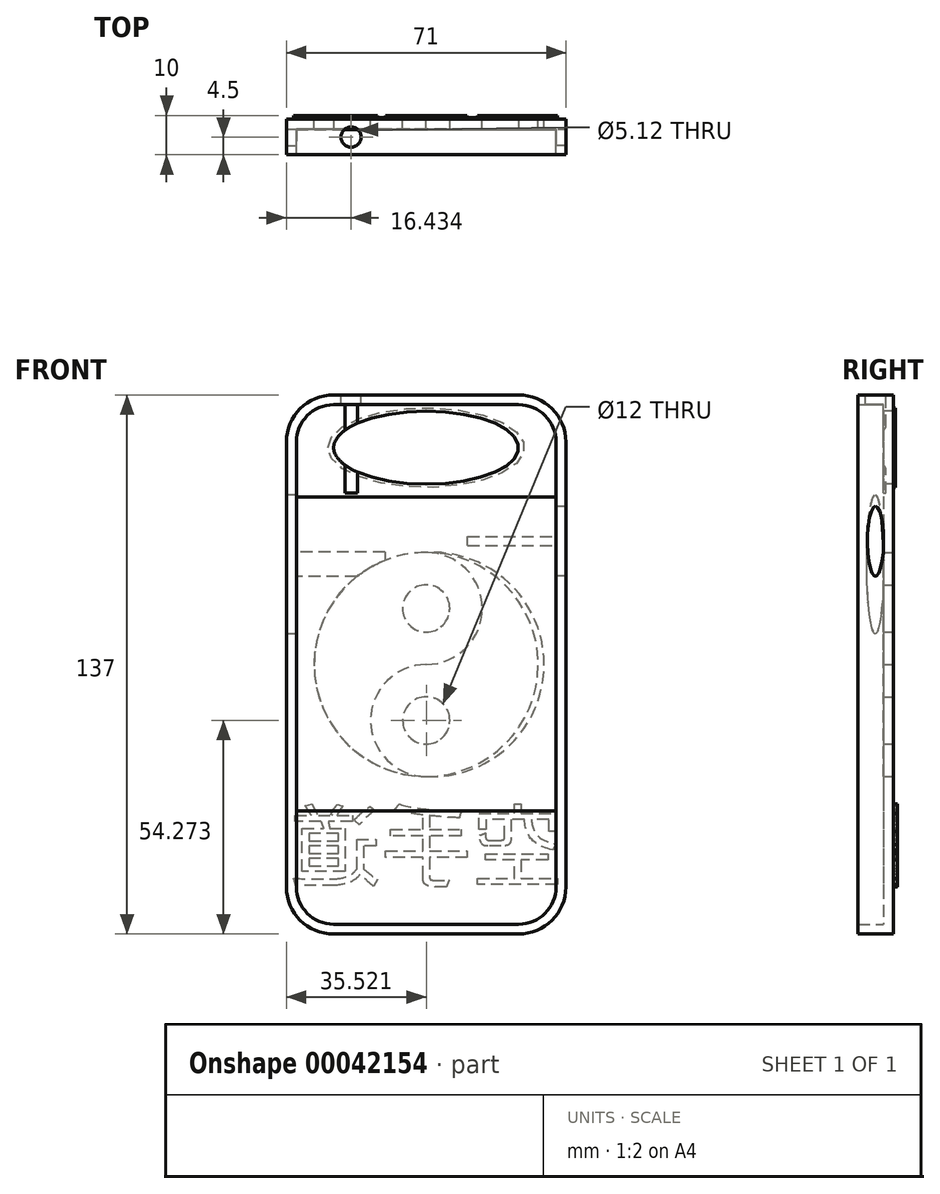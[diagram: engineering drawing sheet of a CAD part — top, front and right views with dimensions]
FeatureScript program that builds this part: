
annotation { "Feature Type Name" : "Feature", "Feature Type Description" : "" }
export const myFeature = defineFeature(function(context is Context, id is Id, definition is map)
    precondition{}
    {
        {
            var Q0;
            Q0=qCreatedBy(makeId("Front.planeOp"),FACE);
            var sketch = newSketch(context, id + "F0", { "sketchPlane" : qUnion([Q0])});
            skLineSegment(sketch, "E0.rect.bottom", {"start": v(35.5, 68.5) * mm, "end": v(-35.5, 68.5) * mm});
            skLineSegment(sketch, "E0.rect.top", {"start": v(35.5, -68.5) * mm, "end": v(-35.5, -68.5) * mm});
            skLineSegment(sketch, "E0.rect.left", {"start": v(35.5, 68.5) * mm, "end": v(35.5, -68.5) * mm});
            skLineSegment(sketch, "E0.rect.right", {"start": v(-35.5, 68.5) * mm, "end": v(-35.5, -68.5) * mm});
            skPoint(sketch, "E0.rect.middle", {"position": v(0, 0) * mm});
            skSolve(sketch);
        }
        {
            var Q0;
            Q0=makeQuery(id+"F0.imprint","IMPRINT",FACE,{"disambiguationData":[TD([[makeQuery(id+"F0.imprint","IMPRINT",EDGE,{"derivedFrom":sQuery(id+"F0.wireOp",EDGE,"E0.rect.bottom")}),1.0]])]});
            extrude(context, id + "F1", {"entities" : qUnion([Q0]), "depth" : 9 * mm});
        }
        {
            var Q0;
            Q0=makeQuery(id+"F1.opExtrude","SWEPT_EDGE",EDGE,{"disambiguationData":[OSD([sQuery(id+"F0.wireOp",EDGE,"E0.rect.bottom"),sQuery(id+"F0.wireOp",EDGE,"E0.rect.left")])]});
            var Q1;
            Q1=makeQuery(id+"F1.opExtrude","SWEPT_EDGE",EDGE,{"disambiguationData":[OSD([sQuery(id+"F0.wireOp",EDGE,"E0.rect.bottom"),sQuery(id+"F0.wireOp",EDGE,"E0.rect.right")])]});
            var Q2;
            Q2=makeQuery(id+"F1.opExtrude","SWEPT_EDGE",EDGE,{"disambiguationData":[OSD([sQuery(id+"F0.wireOp",EDGE,"E0.rect.top"),sQuery(id+"F0.wireOp",EDGE,"E0.rect.left")])]});
            var Q3;
            Q3=makeQuery(id+"F1.opExtrude","SWEPT_EDGE",EDGE,{"disambiguationData":[OSD([sQuery(id+"F0.wireOp",EDGE,"E0.rect.top"),sQuery(id+"F0.wireOp",EDGE,"E0.rect.right")])]});
            fillet(context, id + "F2", {"entities" : qUnion([Q0, Q1, Q2, Q3]), "radius" : 12 * mm, "tangentPropagation" : true, "allowEdgeOverflow" : false});
        }
        {
            var Q0;
            Q0=makeQuery(id+"F1.opExtrude","CAP_FACE",FACE,{"disambiguationData":[OSD([sQuery(id+"F0.wireOp",EDGE,"E0.rect.bottom"),sQuery(id+"F0.wireOp",EDGE,"E0.rect.top"),sQuery(id+"F0.wireOp",EDGE,"E0.rect.left"),sQuery(id+"F0.wireOp",EDGE,"E0.rect.right")])],"isStart":false});
            shell(context, id + "F3", {"entities" : qUnion([Q0]), "thickness" : 2.5 * mm});
        }
        {
            var Q0;
            Q0=makeQuery(id+"F1.opExtrude","SWEPT_FACE",FACE,{"disambiguationData":[OSD([sQuery(id+"F0.wireOp",EDGE,"E0.rect.bottom")])]});
            var sketch = newSketch(context, id + "F4", { "sketchPlane" : qUnion([Q0])});
            skLineSegment(sketch, "E1", {"start": v(0, 0) * mm, "end": v(0, -9) * mm});
            skLineSegment(sketch, "E2", {"start": v(-35.72, -4.5) * mm, "end": v(0, -4.5) * mm});
            skPoint(sketch, "E2.startSnap0", {"position": v(-23.5, -4.5) * mm});
            skPoint(sketch, "E3", {"position": v(-19.07, -4.5) * mm});
            skCircle(sketch, "E4", {"center": v(-19.07, -4.5) * mm, "radius": 2.56 * mm});
            skSolve(sketch);
        }
        {
            var Q0;
            Q0 = qSketchRegion(id + "F4", true);
            extrude(context, id + "F5", {"entities" : qUnion([Q0]), "operationType" : NewBodyOperationType.REMOVE, "oppositeDirection" : true, "depth" : 25 * mm});
        }
        {
            var Q0;
            Q0=makeQuery(id+"F1.opExtrude","SWEPT_FACE",FACE,{"disambiguationData":[OSD([sQuery(id+"F0.wireOp",EDGE,"E0.rect.right")])]});
            var sketch = newSketch(context, id + "F6", { "sketchPlane" : qUnion([Q0])});
            skEllipse(sketch, "E5", {"center": v(4.62, 25.44) * mm, "majorRadius": 17.66 * mm, "minorRadius": 2.16 * mm, "majorAxis": v(0, 1)});
            skSolve(sketch);
        }
        {
            var Q0;
            Q0 = qSketchRegion(id + "F6", true);
            extrude(context, id + "F7", {"entities" : qUnion([Q0]), "operationType" : NewBodyOperationType.REMOVE, "oppositeDirection" : true, "depth" : 25 * mm});
        }
        {
            var Q0;
            Q0=makeQuery(id+"F1.opExtrude","CAP_FACE",FACE,{"disambiguationData":[OSD([sQuery(id+"F0.wireOp",EDGE,"E0.rect.bottom"),sQuery(id+"F0.wireOp",EDGE,"E0.rect.top"),sQuery(id+"F0.wireOp",EDGE,"E0.rect.left"),sQuery(id+"F0.wireOp",EDGE,"E0.rect.right")])],"isStart":true});
            var sketch = newSketch(context, id + "F8", { "sketchPlane" : qUnion([Q0])});
            skEllipse(sketch, "E6", {"center": v(0, 55.09) * mm, "majorRadius": 23.5 * mm, "minorRadius": 9.28 * mm, "majorAxis": v(1, 0)});
            skEllipse(sketch, "E7", {"center": v(0, 55.09) * mm, "majorRadius": 24.96 * mm, "minorRadius": 10.1 * mm, "majorAxis": v(1, 0)});
            skSolve(sketch);
        }
        {
            var Q0;
            Q0=makeQuery(id+"F8.imprint","IMPRINT",FACE,{"disambiguationData":[TD([[makeQuery(id+"F8.imprint","IMPRINT",EDGE,{"derivedFrom":sQuery(id+"F8.wireOp",EDGE,"E6")}),-1.0]])]});
            extrude(context, id + "F9", {"entities" : qUnion([Q0]), "operationType" : NewBodyOperationType.ADD, "depth" : 0.5 * mm});
        }
        {
            var Q0;
            Q0=makeQuery(id+"F9.boolean.opBoolean","SPLIT",FACE,{"disambiguationData":[TD([makeQuery(id+"F9.opExtrude","SWEPT_FACE",FACE,{"disambiguationData":[OSD([sQuery(id+"F8.wireOp",EDGE,"E6")])]})])],"derivedFrom":makeQuery(id+"F1.opExtrude","CAP_FACE",FACE,{"disambiguationData":[OSD([sQuery(id+"F0.wireOp",EDGE,"E0.rect.bottom"),sQuery(id+"F0.wireOp",EDGE,"E0.rect.top"),sQuery(id+"F0.wireOp",EDGE,"E0.rect.left"),sQuery(id+"F0.wireOp",EDGE,"E0.rect.right")])],"isStart":true})});
            extrude(context, id + "F10", {"entities" : qUnion([Q0]), "operationType" : NewBodyOperationType.REMOVE, "oppositeDirection" : true, "depth" : 25 * mm});
        }
        {
            var Q0;
            Q0=makeQuery(id+"F1.opExtrude","SWEPT_FACE",FACE,{"disambiguationData":[OSD([sQuery(id+"F0.wireOp",EDGE,"E0.rect.left")])]});
            var sketch = newSketch(context, id + "F11", { "sketchPlane" : qUnion([Q0])});
            skEllipse(sketch, "E8", {"center": v(-4.56, 31.33) * mm, "majorRadius": 8.87 * mm, "minorRadius": 2.08 * mm, "majorAxis": v(0, 1)});
            skSolve(sketch);
        }
        {
            var Q0;
            Q0 = qSketchRegion(id + "F11", true);
            extrude(context, id + "F12", {"entities" : qUnion([Q0]), "operationType" : NewBodyOperationType.REMOVE, "oppositeDirection" : true, "depth" : 25 * mm});
        }
        {
            var Q0;
            {var subQ0=sQuery(id+"F0.wireOp",EDGE,"E0.rect.bottom");var subQ1=sQuery(id+"F0.wireOp",EDGE,"E0.rect.top");var subQ2=sQuery(id+"F0.wireOp",EDGE,"E0.rect.left");var subQ3=sQuery(id+"F0.wireOp",EDGE,"E0.rect.right");Q0=makeQuery(id+"F9.boolean.opBoolean","SPLIT",FACE,{"disambiguationData":[TD([makeQuery(id+"F1.opExtrude","SWEPT_FACE",FACE,{"disambiguationData":[OSD([subQ0])]})])],"derivedFrom":makeQuery(id+"F1.opExtrude","CAP_FACE",FACE,{"disambiguationData":[OSD([subQ0,subQ1,subQ2,subQ3])],"isStart":true})});}
            var sketch = newSketch(context, id + "F13", { "sketchPlane" : qUnion([Q0])});
            skArc(sketch, "E9", {"start": v(0, 28.45) * mm, "mid": v(-28.45, 0) * mm, "end": v(0, -28.45) * mm});
            skLineSegment(sketch, "E10", {"start": v(0, 28.45) * mm, "end": v(0, -28.45) * mm, "construction": true});
            skArc(sketch, "E11", {"start": v(0, 0) * mm, "mid": v(14.23, 14.23) * mm, "end": v(0, 28.45) * mm, "construction": true});
            skArc(sketch, "E12", {"start": v(0, 0) * mm, "mid": v(-14.25, -14.23) * mm, "end": v(0, -28.45) * mm, "construction": true});
            skArc(sketch, "E13", {"start": v(0, 28.45) * mm, "mid": v(-14.23, 14.23) * mm, "end": v(0, 0) * mm});
            skArc(sketch, "E14", {"start": v(0, -28.45) * mm, "mid": v(14.12, -14.23) * mm, "end": v(0, 0) * mm});
            skCircle(sketch, "E15", {"center": v(0, 14.23) * mm, "radius": 6 * mm});
            skCircle(sketch, "E16", {"center": v(-0.02, -14.23) * mm, "radius": 6 * mm});
            skArc(sketch, "E17", {"start": v(0, 28.45) * mm, "mid": v(28.45, 0) * mm, "end": v(0, -28.45) * mm});
            skSolve(sketch);
        }
        {
            var Q0;
            Q0=makeQuery(id+"F13.imprint","IMPRINT",FACE,{"disambiguationData":[TD([[makeQuery(id+"F13.imprint","IMPRINT",EDGE,{"derivedFrom":sQuery(id+"F13.wireOp",EDGE,"E13")}),1.0]])]});
            var Q1;
            Q1=makeQuery(id+"F13.imprint","IMPRINT",FACE,{"disambiguationData":[TD([[makeQuery(id+"F13.imprint","IMPRINT",EDGE,{"derivedFrom":sQuery(id+"F13.wireOp",EDGE,"E16")}),1.0]])]});
            extrude(context, id + "F14", {"entities" : qUnion([Q0, Q1]), "operationType" : NewBodyOperationType.REMOVE, "oppositeDirection" : true, "depth" : 25 * mm});
        }
        {
            var Q0;
            {var subQ0=sQuery(id+"F0.wireOp",EDGE,"E0.rect.bottom");var subQ1=sQuery(id+"F0.wireOp",EDGE,"E0.rect.top");var subQ2=sQuery(id+"F0.wireOp",EDGE,"E0.rect.left");var subQ3=sQuery(id+"F0.wireOp",EDGE,"E0.rect.right");var subQ5=makeQuery(id+"F1.opExtrude","SWEPT_FACE",FACE,{"disambiguationData":[OSD([subQ0])]});Q0=makeQuery(id+"F14.boolean.opBoolean","SPLIT",FACE,{"disambiguationData":[TD([subQ5])],"derivedFrom":makeQuery(id+"F9.boolean.opBoolean","SPLIT",FACE,{"disambiguationData":[TD([subQ5])],"derivedFrom":makeQuery(id+"F1.opExtrude","CAP_FACE",FACE,{"disambiguationData":[OSD([subQ0,subQ1,subQ2,subQ3])],"isStart":true})})});}
            var sketch = newSketch(context, id + "F15", { "sketchPlane" : qUnion([Q0])});
            skPoint(sketch, "E18", {"position": v(0, 28.45) * mm});
            skArc(sketch, "E19", {"start": v(0, 28.45) * mm, "mid": v(-28.45, 0) * mm, "end": v(0, -28.45) * mm});
            skPoint(sketch, "E19.second.point", {"position": v(0, -28.45) * mm});
            skPoint(sketch, "E19.third.point", {"position": v(28.45, 0) * mm});
            skArc(sketch, "E20", {"start": v(0, 28.45) * mm, "mid": v(-29.95, 0) * mm, "end": v(0, -28.45) * mm});
            skSolve(sketch);
        }
        {
            var Q0;
            Q0=makeQuery(id+"F15.imprint","IMPRINT",FACE,{"disambiguationData":[TD([[makeQuery(id+"F15.imprint","IMPRINT",EDGE,{"derivedFrom":sQuery(id+"F15.wireOp",EDGE,"E19")}),-1.0]])]});
            extrude(context, id + "F16", {"entities" : qUnion([Q0]), "operationType" : NewBodyOperationType.REMOVE, "endBound" : BoundingType.SYMMETRIC, "oppositeDirection" : true, "depth" : 25 * mm});
        }
        {
            var Q0;
            {var subQ0=sQuery(id+"F0.wireOp",EDGE,"E0.rect.bottom");var subQ1=sQuery(id+"F0.wireOp",EDGE,"E0.rect.top");var subQ2=sQuery(id+"F0.wireOp",EDGE,"E0.rect.left");var subQ3=sQuery(id+"F0.wireOp",EDGE,"E0.rect.right");var subQ5=makeQuery(id+"F1.opExtrude","SWEPT_FACE",FACE,{"disambiguationData":[OSD([subQ0])]});Q0=makeQuery(id+"F16.boolean.opBoolean","SPLIT",FACE,{"disambiguationData":[TD([subQ5])],"derivedFrom":makeQuery(id+"F14.boolean.opBoolean","SPLIT",FACE,{"disambiguationData":[TD([subQ5])],"derivedFrom":makeQuery(id+"F9.boolean.opBoolean","SPLIT",FACE,{"disambiguationData":[TD([subQ5])],"derivedFrom":makeQuery(id+"F1.opExtrude","CAP_FACE",FACE,{"disambiguationData":[OSD([subQ0,subQ1,subQ2,subQ3])],"isStart":true})})})});}
            var sketch = newSketch(context, id + "F17", { "sketchPlane" : qUnion([Q0])});
            skText(sketch, "E21", { "text": "空手道\n\n", "fontName": "NotoSansCJKjp-Regular.otf"});
            const initialGuessF17  = {"E21": [-0.03475, -0.0548, 1, 0, 0.01665]};
            skSetInitialGuess(sketch, initialGuessF17);
            skSolve(sketch);
        }
        {
            var Q0;
            Q0 = qSketchRegion(id + "F17", true);
            extrude(context, id + "F18", {"entities" : qUnion([Q0]), "operationType" : NewBodyOperationType.ADD, "depth" : 1 * mm});
        }
        {
            var Q0;
            {var subQ0=sQuery(id+"F0.wireOp",EDGE,"E0.rect.bottom");var subQ1=sQuery(id+"F0.wireOp",EDGE,"E0.rect.top");var subQ2=sQuery(id+"F0.wireOp",EDGE,"E0.rect.left");var subQ3=sQuery(id+"F0.wireOp",EDGE,"E0.rect.right");var subQ18=makeQuery(id+"F3.opShell","OFFSET_FACE",FACE,{"disambiguationData":[OSD([subQ0])]});Q0=makeQuery(id+"F16.boolean.opBoolean","SPLIT",FACE,{"disambiguationData":[TD([subQ18])],"derivedFrom":makeQuery(id+"F14.boolean.opBoolean","SPLIT",FACE,{"disambiguationData":[TD([subQ18])],"derivedFrom":makeQuery(id+"F3.opShell","OFFSET_FACE",FACE,{"disambiguationData":[OSD([subQ0,subQ1,subQ2,subQ3])]})})});}
            var sketch = newSketch(context, id + "F19", { "sketchPlane" : qUnion([Q0])});
            skLineSegment(sketch, "E22.bottom", {"start": v(-33, 42.54) * mm, "end": v(33, 42.54) * mm});
            skLineSegment(sketch, "E22.top", {"start": v(-33, -37.2) * mm, "end": v(33, -37.2) * mm});
            skLineSegment(sketch, "E22.left", {"start": v(-33, 42.54) * mm, "end": v(-33, -37.2) * mm});
            skLineSegment(sketch, "E22.right", {"start": v(33, 42.54) * mm, "end": v(33, -37.2) * mm});
            skSolve(sketch);
        }
        {
            var Q0;
            Q0 = qSketchRegion(id + "F19", true);
            extrude(context, id + "F20", {"entities" : qUnion([Q0]), "depth" : 0.1 * mm});
        }
    });
